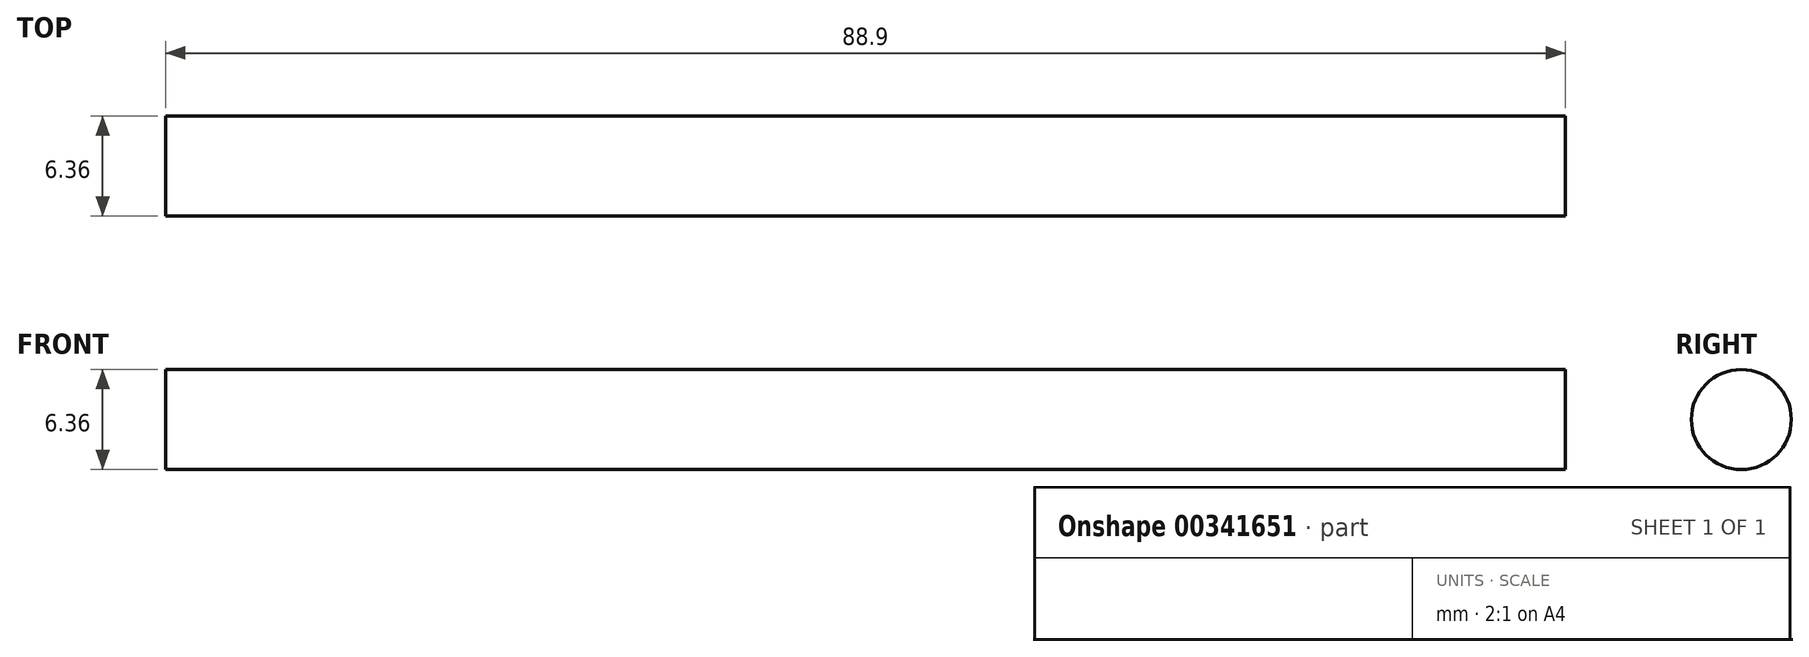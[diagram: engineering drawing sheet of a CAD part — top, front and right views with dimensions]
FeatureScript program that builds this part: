
annotation { "Feature Type Name" : "Feature", "Feature Type Description" : "" }
export const myFeature = defineFeature(function(context is Context, id is Id, definition is map)
    precondition{}
    {
        {
            var Q0;
            Q0=qCreatedBy(makeId("Right.planeOp"),FACE);
            var sketch = newSketch(context, id + "F0", { "sketchPlane" : qUnion([Q0])});
            skCircle(sketch, "E0", {"center": v(0, 0) * mm, "radius": 3.18 * mm});
            skSolve(sketch);
        }
        {
            var Q0;
            Q0 = qSketchRegion(id + "F0", true);
            extrude(context, id + "F1", {"entities" : qUnion([Q0]), "depth" : 88.9 * mm});
        }
    });
